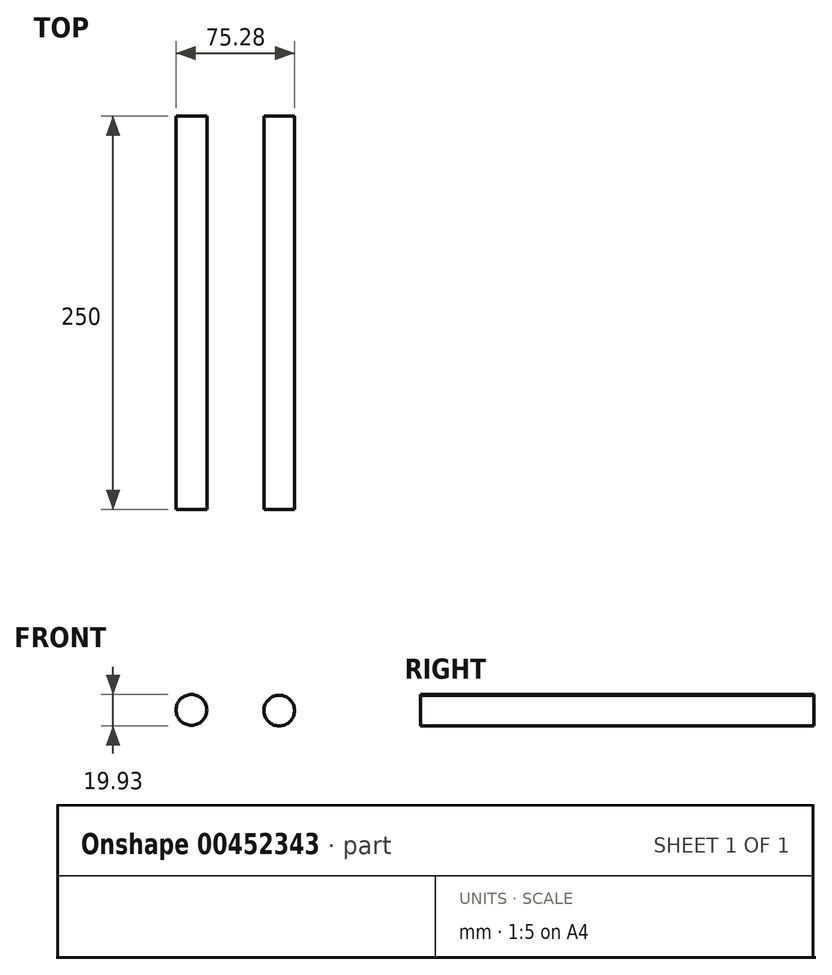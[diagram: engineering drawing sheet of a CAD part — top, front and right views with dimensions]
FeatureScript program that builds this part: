
annotation { "Feature Type Name" : "Feature", "Feature Type Description" : "" }
export const myFeature = defineFeature(function(context is Context, id is Id, definition is map)
    precondition{}
    {
        {
            var Q0;
            Q0=qCreatedBy(makeId("Front.planeOp"),FACE);
            var sketch = newSketch(context, id + "F0", { "sketchPlane" : qUnion([Q0])});
            skCircle(sketch, "E0", {"center": v(0, 0) * mm, "radius": 9.76 * mm});
            skCircle(sketch, "E1", {"center": v(-55.75, 0.4) * mm, "radius": 9.76 * mm});
            skSolve(sketch);
        }
        {
            var Q0;
            Q0 = qSketchRegion(id + "F0", true);
            extrude(context, id + "F1", {"entities" : qUnion([Q0]), "oppositeDirection" : true, "depth" : 250 * mm});
        }
    });
